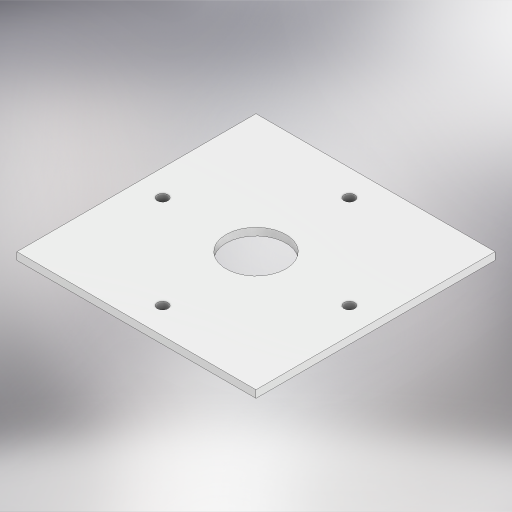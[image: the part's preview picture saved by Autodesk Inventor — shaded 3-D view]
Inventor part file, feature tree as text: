
AUTODESK INVENTOR PART (.ipt)
format: ipt  version: 2024 (Build 280153000, 153)  size: 283,136 bytes
history: native  units: in
note: dims shown in document units (in); Inventor stores cm internally (conversion verified against a paired STEP export)
features: extrude x1, sketch x1
ambient origin geometry x8: Origin, YZ Plane, XZ Plane, XY Plane, X Axis, Y Axis, Z Axis, Center Point
bodies: Solid1 (feature_tree)
feature tree (2):
  extrude  "Extrusion1"  Depth=4.0in
  sketch  "Sketch1"  dims[d0=4.0in d1=4.0in d2=0.18in d3=0.4375in d4=1.0in d5=1.5748in d7=360.0deg d9=0.125in d10=0.0in]
